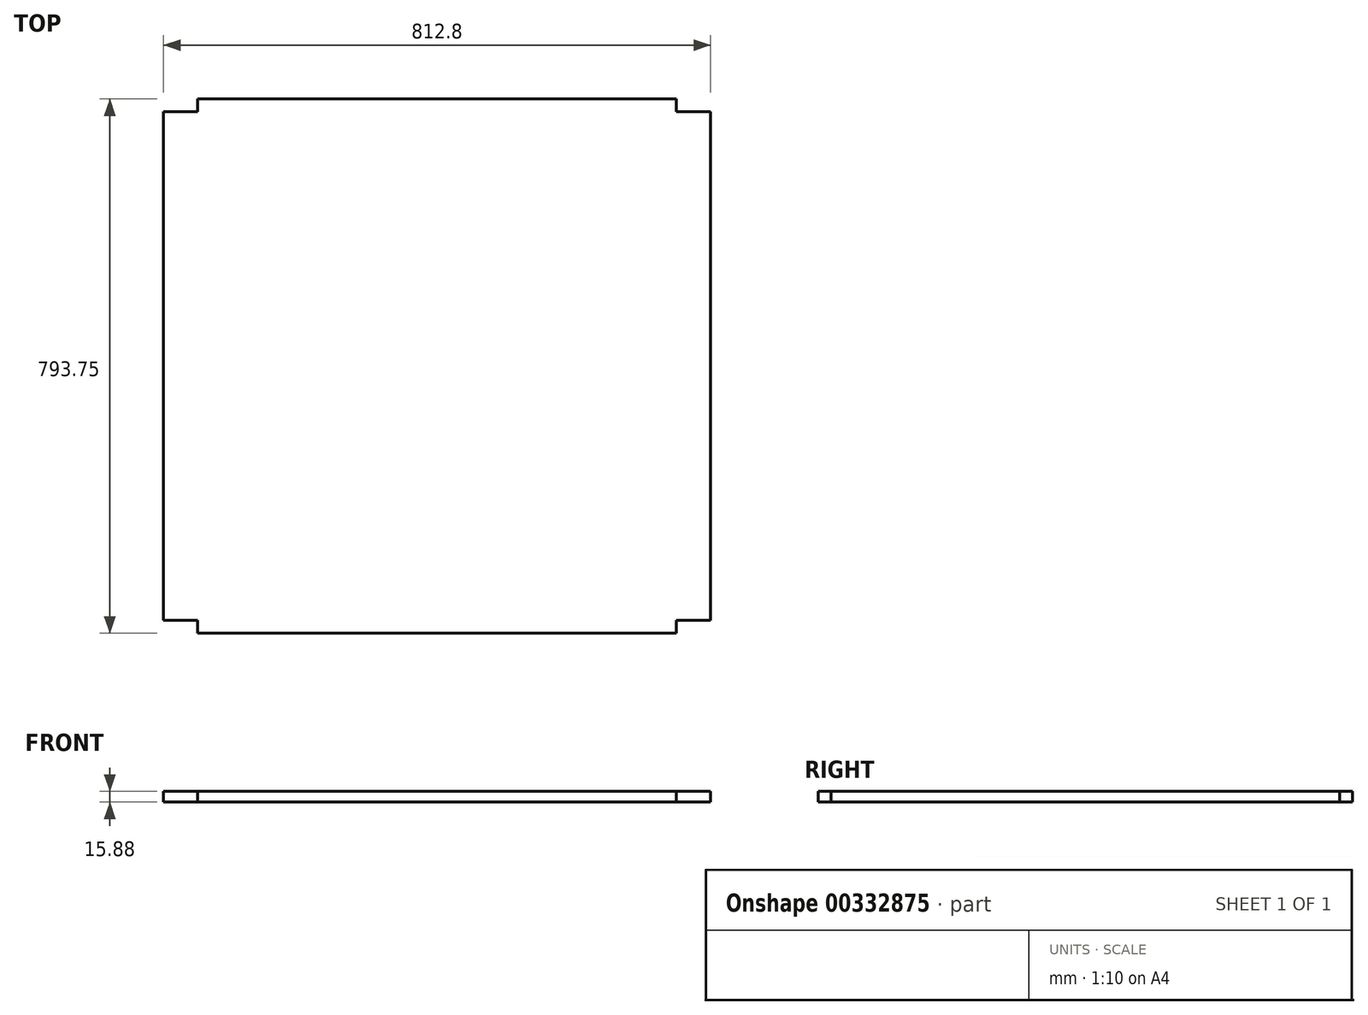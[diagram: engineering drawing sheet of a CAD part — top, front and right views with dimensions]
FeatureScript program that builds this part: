
annotation { "Feature Type Name" : "Feature", "Feature Type Description" : "" }
export const myFeature = defineFeature(function(context is Context, id is Id, definition is map)
    precondition{}
    {
        {
            var Q0;
            Q0=qCreatedBy(makeId("Top.planeOp"),FACE);
            var sketch = newSketch(context, id + "F0", { "sketchPlane" : qUnion([Q0])});
            skLineSegment(sketch, "E0.bottom", {"start": v(-355.6, -140.34) * mm, "end": v(355.6, -140.34) * mm});
            skLineSegment(sketch, "E0.left", {"start": v(-406.4, -121.29) * mm, "end": v(-406.4, 634.36) * mm});
            skLineSegment(sketch, "E0.right", {"start": v(406.4, -121.29) * mm, "end": v(406.4, 634.36) * mm});
            skPoint(sketch, "E0.middle", {"position": v(0, 0) * mm});
            skLineSegment(sketch, "E1.top", {"start": v(-406.4, 634.36) * mm, "end": v(-355.6, 634.36) * mm});
            skLineSegment(sketch, "E1.right", {"start": v(-355.6, 653.41) * mm, "end": v(-355.6, 634.36) * mm});
            skLineSegment(sketch, "E2.bottom", {"start": v(-355.6, -121.29) * mm, "end": v(-406.4, -121.29) * mm});
            skLineSegment(sketch, "E2.left", {"start": v(-355.6, -121.29) * mm, "end": v(-355.6, -140.34) * mm});
            skLineSegment(sketch, "E3.top", {"start": v(406.4, 634.36) * mm, "end": v(355.6, 634.36) * mm});
            skLineSegment(sketch, "E3.right", {"start": v(355.6, 653.41) * mm, "end": v(355.6, 634.36) * mm});
            skLineSegment(sketch, "E4.bottom", {"start": v(355.6, -121.29) * mm, "end": v(406.4, -121.29) * mm});
            skLineSegment(sketch, "E4.left", {"start": v(355.6, -121.29) * mm, "end": v(355.6, -140.34) * mm});
            skPoint(sketch, "E5.trimOffspring.end.orphan", {"position": v(406.4, 140.34) * mm});
            skPoint(sketch, "E6.orphan", {"position": v(406.4, -140.34) * mm});
            skPoint(sketch, "E7.orphan", {"position": v(-406.4, -140.34) * mm});
            skPoint(sketch, "E8.orphan", {"position": v(-406.4, 140.34) * mm});
            skLineSegment(sketch, "E9", {"start": v(355.6, 653.41) * mm, "end": v(-355.6, 653.41) * mm});
            skSolve(sketch);
        }
        {
            var Q0;
            Q0 = qSketchRegion(id + "F0", true);
            extrude(context, id + "F1", {"entities" : qUnion([Q0]), "depth" : 15.88 * mm});
        }
    });
